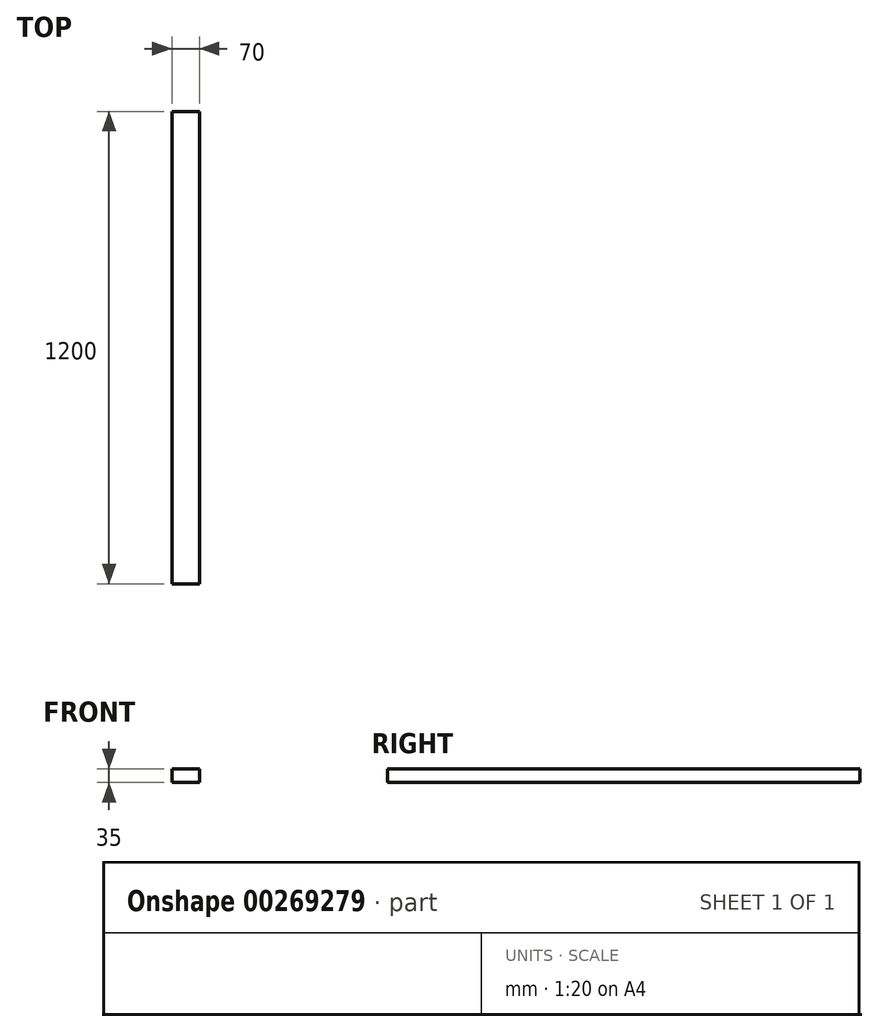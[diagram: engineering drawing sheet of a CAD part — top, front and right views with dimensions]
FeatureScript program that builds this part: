
annotation { "Feature Type Name" : "Feature", "Feature Type Description" : "" }
export const myFeature = defineFeature(function(context is Context, id is Id, definition is map)
    precondition{}
    {
        {
            var Q0;
            Q0=qCreatedBy(makeId("Front.planeOp"),FACE);
            var sketch = newSketch(context, id + "F0", { "sketchPlane" : qUnion([Q0])});
            skLineSegment(sketch, "E0.bottom", {"start": v(-35, 17.26) * mm, "end": v(35, 17.26) * mm});
            skLineSegment(sketch, "E0.top", {"start": v(-35, -17.74) * mm, "end": v(35, -17.74) * mm});
            skLineSegment(sketch, "E0.left", {"start": v(-35, 17.26) * mm, "end": v(-35, -17.74) * mm});
            skLineSegment(sketch, "E0.right", {"start": v(35, 17.26) * mm, "end": v(35, -17.74) * mm});
            skSolve(sketch);
        }
        {
            assignVariable(context, id + "F1", {"name" : "Length", "anyValue" : 1200});
        }
        {
            var Q0;
            Q0=qSketchRegion(id+"F0",true);
            extrude(context, id + "F2", {"entities" : qUnion([Q0]), "depth" : (getVariable(context, 'Length')) * mm});
        }
    });
